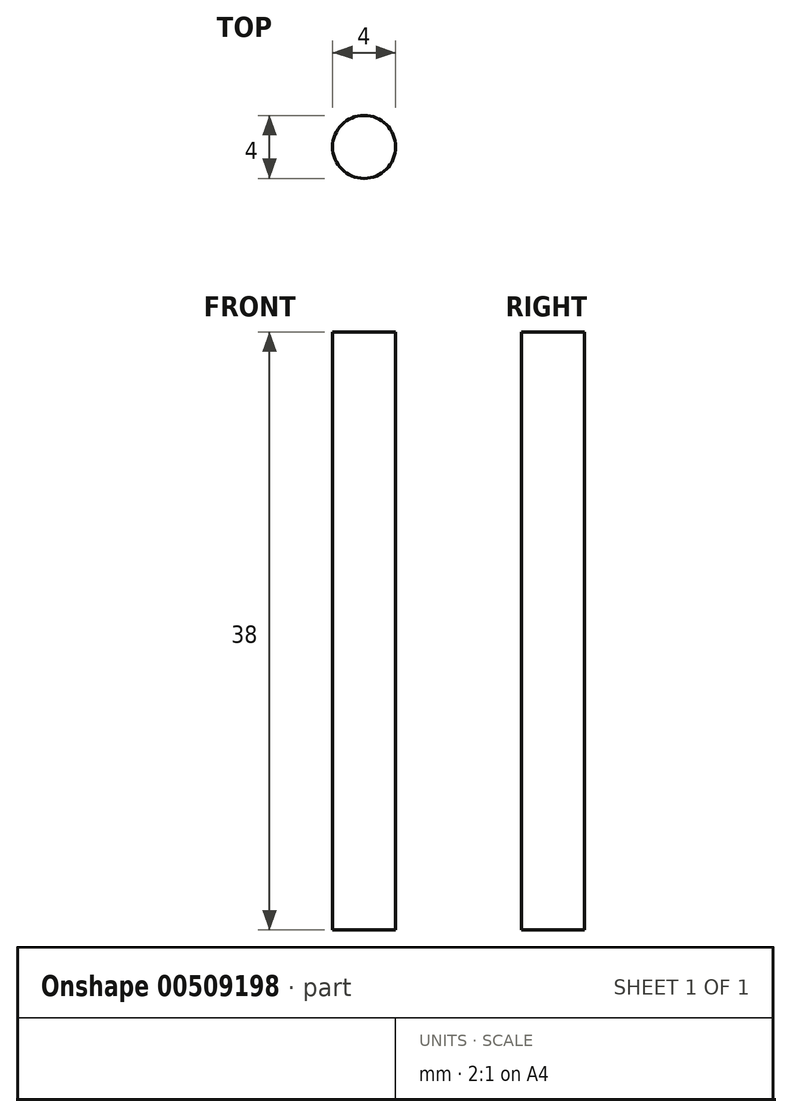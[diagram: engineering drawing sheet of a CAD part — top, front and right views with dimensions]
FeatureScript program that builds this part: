
annotation { "Feature Type Name" : "Feature", "Feature Type Description" : "" }
export const myFeature = defineFeature(function(context is Context, id is Id, definition is map)
    precondition{}
    {
        {
            var Q0;
            Q0=qCreatedBy(makeId("Top.planeOp"),FACE);
            var sketch = newSketch(context, id + "F0", { "sketchPlane" : qUnion([Q0])});
            skCircle(sketch, "E0", {"center": v(0, 0) * mm, "radius": 2 * mm});
            skSolve(sketch);
        }
        {
            var Q0;
            Q0=makeQuery(id+"F0.imprint","IMPRINT",FACE,{"disambiguationData":[TD([[makeQuery(id+"F0.imprint","IMPRINT",EDGE,{"derivedFrom":sQuery(id+"F0.wireOp",EDGE,"E0")}),1.0]])]});
            extrude(context, id + "F1", {"entities" : qUnion([Q0]), "depth" : 38 * mm});
        }
    });
